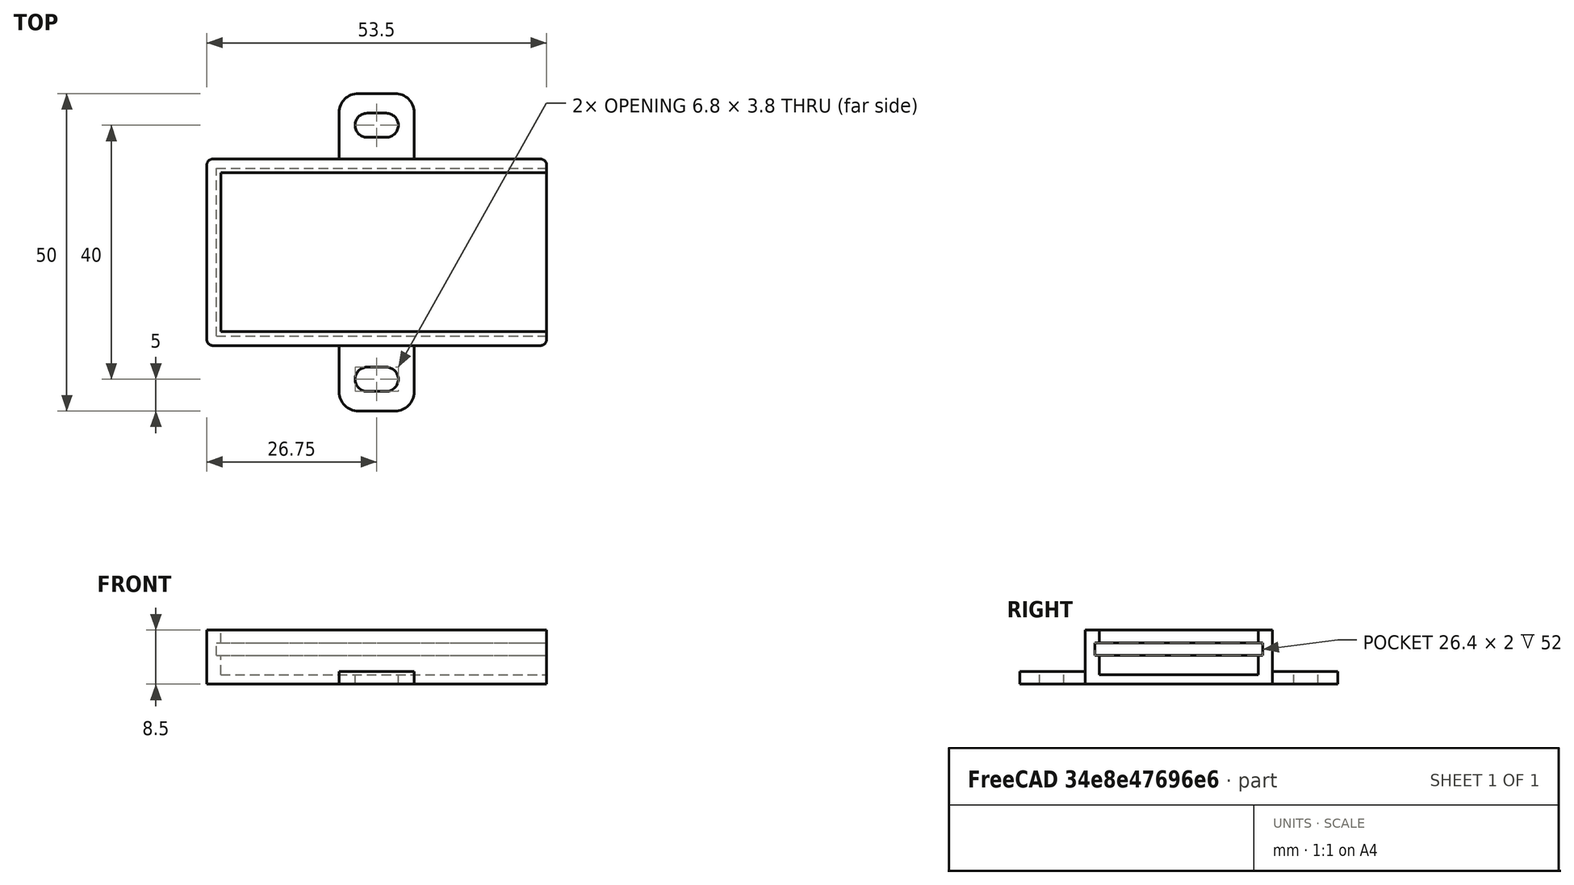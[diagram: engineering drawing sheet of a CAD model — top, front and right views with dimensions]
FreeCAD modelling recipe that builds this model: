
FCSTD DOCUMENT  (FreeCAD 0.19R)
Label: step_down_xl4015e1_51x26
License: FreeArt
LicenseURL: http://artlibre.org/licence/lal
objects: Part::Box×3, Part::MultiFuse×2, Spreadsheet::Sheet×1, Part::Fillet×1, Part::Feature×1, Part::Cut×1, App::Part×1
note: 8 computed .brp shape members not serialized (recipe doc carries the construction recipe); baked Part::Feature solids carry a one-line shape summary decoded from their .brp

FEATURE [Spreadsheet::Sheet] Spreadsheet  label="p"
  cells = A1=pcb_x; B1(pcb_x)=52; A2=pcb_y; B2(pcb_y)=26.4; A3=pcb_z; B3(pcb_z)=2; A4=pcb_under; B4(pcb_under)=3; A5=side_wall; B5(side_wall)=1.5; A6=pcb_side_lane; B6(pcb_side_lane)=0.7; A7=bottom_wall; B7(bottom_wall)=1.5; A8=pcb_above; B8(pcb_above)=2
FEATURE [Part::Box] Box  label="external cube"
  AttacherType = Attacher::AttachEngine3D
  Height = 8.5
  Length = 53.5
  Width = 29.4
  expr: Length = <<p>>.pcb_x + <<p>>.side_wall
  expr: Width = <<p>>.pcb_y + 2 * <<p>>.side_wall
  expr: Height = <<p>>.bottom_wall + <<p>>.pcb_under + <<p>>.pcb_z + <<p>>.pcb_above
FEATURE [Part::Box] Box006  label="internal cube"
  AttacherType = Attacher::AttachEngine3D
  Height = 7
  Length = 52.1
  Placement = pos=(2.2,2.2,1.5) rot=(0,0,1;0rad)
  Width = 25
  expr: Length = <<p>>.pcb_x - 2 * <<p>>.pcb_side_lane + <<p>>.side_wall
  expr: Width = <<p>>.pcb_y - 2 * <<p>>.pcb_side_lane
  expr: Height = <<p>>.pcb_under + <<p>>.pcb_z + <<p>>.pcb_above
  expr: .Placement.Base.z = <<p>>.bottom_wall
  expr: .Placement.Base.x = <<p>>.side_wall + <<p>>.pcb_side_lane
  expr: .Placement.Base.y = <<p>>.side_wall + <<p>>.pcb_side_lane
FEATURE [Part::Box] Box007  label="pcb extract cube"
  AttacherType = Attacher::AttachEngine3D
  Height = 2
  Length = 52
  Placement = pos=(1.5,1.5,4.5) rot=(0,0,1;0rad)
  Width = 26.4
  expr: Height = <<p>>.pcb_z
  expr: .Placement.Base.z = <<p>>.bottom_wall + <<p>>.pcb_under
  expr: Width = <<p>>.pcb_y
  expr: Length = <<p>>.pcb_x
  expr: .Placement.Base.x = <<p>>.side_wall
  expr: .Placement.Base.y = <<p>>.side_wall
FEATURE [Part::MultiFuse] Fusion  label="extract fusion"
  Shapes = -> [Box006,Box007]
FEATURE [Part::Fillet] Fillet  label="external fillet"
  Base = -> Box
  Edges = 4 edges r=1: [Edge1,Edge3,Edge5,Edge7]
FEATURE [Part::Feature] Cut002001  label="attach plane y dir001"
  Placement = pos=(20.85,-10.3,0) rot=(0,0,1;0rad)
  shape: bbox 11.8 x 50 x 2 mm, 20 faces (baked)
FEATURE [Part::MultiFuse] Fusion001  label="solid fusion"
  Shapes = -> [Fillet,Cut002001]
FEATURE [Part::Cut] Cut  label="body cut"
  Base = -> Fusion001
  Tool = -> Fusion
FEATURE [App::Part] Part  label="pcb box part"
  Group = -> [Box,Fillet,Fusion001,Fusion,Box007,Box006,Cut]
  Origin = -> Origin
